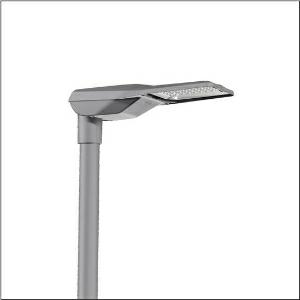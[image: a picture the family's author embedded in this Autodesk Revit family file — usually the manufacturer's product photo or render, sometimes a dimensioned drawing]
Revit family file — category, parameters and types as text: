
# Revit family: streetlight_sl_21_iq_mini___st0_8a_5xe2c41d08gb_f485
name_source: partatom
category: Lighting Fixtures
units: mm (PartAtom-declared; Revit-internal decimal feet)

## family parameters
Cut with Voids When Loaded = No
Host = Face
Light Source = No
Part Type = Normal
Room Calculation Point = No
Round Connector Dimension = Use Diameter
Shared = No

## types (1)
- --- (1 x LED, 5920 lm, 37.1 W, 4000K)
    Apparent Load = 37 VA
    CIE Flux Codes = 38 75 97 100 100
    Color Rendering = 70
    Color Temperature = 4000K
    Default Elevation = 1800 mm
    Description = Streetlight SL 21 iQ mini, mast luminaire, primary light control with lens, of PMMA, primary optical cover: cover, of toughened safety glass, transparent, light distribution: ST0.8a, light emission: direct distribution, primary light characteristic: asymmetric, installation type: post-top, side-entry, LED, High Power LED, rated luminous flux: 5.920lm, luminous efficacy: 160lm/W, light colour: 740, colour temperature: 4000K, control gear: iQ-Comfort, control: Auto-Match, Temp-Guard, Lumen-Switch, Night-Set, Smart-Wire, Light-Fading, Desk-Remote (wireless, voltage-free reading and setting of iQ features in the workshop via application-optimized NFC function/RFID function), optimised constant luminous flux control (CLO 2.0), pre-setting: linear dimming characteristic, mains connection: 220..240V, AC, 50/60Hz, start of lifetime: 37W, end of service life: 39W, reduction: 18W, luminaire housing, of diecast aluminium, powder-coated, Siteco® metallic grey (DB 702S), corrosivity category C5 mid according to DIN EN ISO 12944, please order mast flange separately, inclination adjustable: 0°, 5°, 10°, 15°, sealing non-destructively replaceable, multi-level sealing system, length: 628mm, width: 235mm, height: 110mm, mast flange for spigot size: 42mm (side-entry): 5XC10008XM4, 60/48mm (side-entry/post-top): 5XC10108XM2, 76/60mm (side-entry/post-top): 5XC10108XM1, mounting height: 4..8m, protection rating (complete): IP66, insulation class (complete): insulation class II (safety insulation), certification: CE, ENEC, ENEC+, VDE, impact resistance: IK10, permissible operating ambient temperature for outdoor applications: -40..+50°C, standard-compliant lighting for roads and squares, packaging unit: 1 piece

Light Distribution: ST0.8a
    Height = 110 mm
    Lamp = 1 x LED
    Lamp Light Flux = 5920 lm
    Lamp Power = 37.1 W
    Lamp count = 1
    Length = 625 mm
    Luminous efficacy = 160 lm/W
    Manufacturer = Siteco
    ModVariant = No
    Model = 5XE2C41D08GB
    Number of Poles = 1
    OnlyDefault = Yes
    Power Factor = 1
    Product Name = Streetlight SL 21 iQ mini | ST0.8a
    Product group = mast luminaire | pylon top
    ProductGroupID = 6100
    Protection Class = Protection class II
    Protection Degree = IP 66
    RLX_Detail_Level = 1
    RLX_Emergency_Light_Flux = 0 lm
    RLX_Emergency_Type = 0
    RLX_Emergency_Type_DB = No
    RlxData = <blob elided: 26353 chars, md5=8af6e2f6>
    Socket = socket
    Standby Power = 0 W
    System Light Flux = 5920 lm
    System Power = 37 W
    Type Comments = factory setting: luminous flux: 100 % | dim-lin: 254 | 385 mA
    Type Image = l_1003519.jpg
    URL = http://relux.com
    VarID = @adj_185640
    Voltage = 0 V
    Weight = 0.00 kg
    Width = 234 mm

## geometry (parser evidence)
native form markers: Blend x4, Sweep x10
no freeform markers — native parametric forms only
